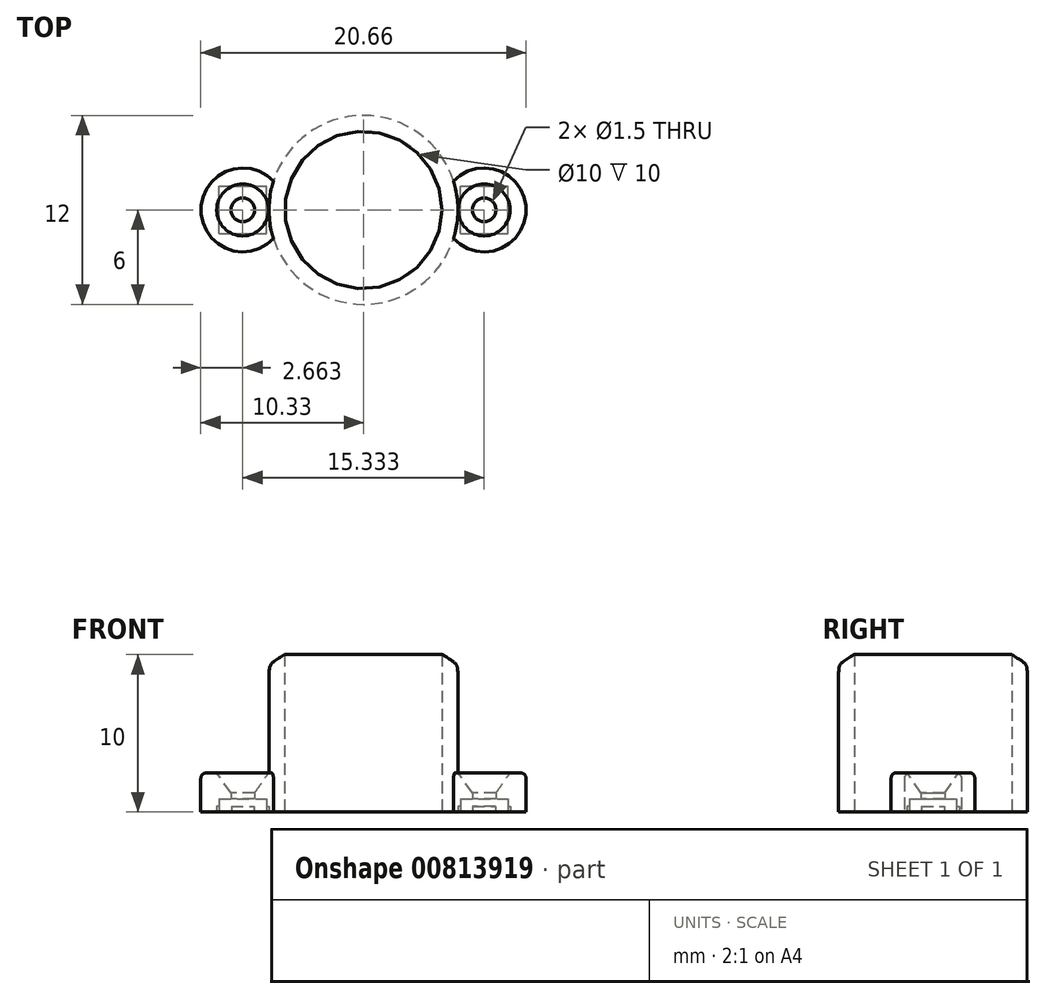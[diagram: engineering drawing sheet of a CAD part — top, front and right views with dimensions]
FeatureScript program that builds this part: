
annotation { "Feature Type Name" : "Feature", "Feature Type Description" : "" }
export const myFeature = defineFeature(function(context is Context, id is Id, definition is map)
    precondition{}
    {
        {
            assignVariable(context, id + "F0", {"name" : "Well", "anyValue" : 10 * mm});
        }
        {
            assignVariable(context, id + "F1", {"name" : "WellHeight", "anyValue" : getVariable(context, 'Well')});
        }
        {
            assignVariable(context, id + "F2", {"name" : "RimHeight", "anyValue" : getVariable(context, 'WellHeight') * 0.25});
        }
        {
            assignVariable(context, id + "F3", {"name" : "Hole", "anyValue" : getVariable(context, 'Well') * 0.15});
        }
        {
            var Q0;
            Q0=qCreatedBy(makeId("Top.planeOp"),FACE);
            var sketch = newSketch(context, id + "F4", { "sketchPlane" : qUnion([Q0])});
            skCircle(sketch, "E0", {"center": v(0, 0) * mm, "radius": 9.33 * mm});
            skCircle(sketch, "E1", {"center": v(0, 0) * mm, "radius": 6 * mm});
            skCircle(sketch, "E2", {"center": v(0, 0) * mm, "radius": 5 * mm});
            skSolve(sketch);
        }
        {
            var Q0;
            Q0=qCreatedBy(makeId("Top.planeOp"),FACE);
            var sketch = newSketch(context, id + "F5", { "sketchPlane" : qUnion([Q0])});
            skCircle(sketch, "E3", {"center": v(0, 0) * mm, "radius": 7.67 * mm});
            skCircle(sketch, "E4", {"center": v(-7.67, 0) * mm, "radius": 0.75 * mm});
            skCircle(sketch, "E5", {"center": v(7.67, 0) * mm, "radius": 0.75 * mm});
            skLineSegment(sketch, "E6.bottom", {"start": v(6.17, -1.5) * mm, "end": v(9.17, -1.5) * mm});
            skLineSegment(sketch, "E6.top", {"start": v(6.17, 1.5) * mm, "end": v(9.17, 1.5) * mm});
            skLineSegment(sketch, "E6.left", {"start": v(6.17, -1.5) * mm, "end": v(6.17, 1.5) * mm});
            skLineSegment(sketch, "E6.right", {"start": v(9.17, -1.5) * mm, "end": v(9.17, 1.5) * mm});
            skLineSegment(sketch, "E7.bottom", {"start": v(-9.17, -1.5) * mm, "end": v(-6.17, -1.5) * mm});
            skLineSegment(sketch, "E7.top", {"start": v(-9.17, 1.5) * mm, "end": v(-6.17, 1.5) * mm});
            skLineSegment(sketch, "E7.left", {"start": v(-9.17, -1.5) * mm, "end": v(-9.17, 1.5) * mm});
            skLineSegment(sketch, "E7.right", {"start": v(-6.17, -1.5) * mm, "end": v(-6.17, 1.5) * mm});
            skSolve(sketch);
        }
        {
            var Q0;
            Q0=qCreatedBy(makeId("Top.planeOp"),FACE);
            var sketch = newSketch(context, id + "F6", { "sketchPlane" : qUnion([Q0])});
            skCircle(sketch, "E8", {"center": v(-7.67, 0) * mm, "radius": 2.67 * mm});
            skCircle(sketch, "E9", {"center": v(7.67, 0) * mm, "radius": 2.67 * mm});
            skCircle(sketch, "E10", {"center": v(-7.67, 0) * mm, "radius": 1.67 * mm});
            skCircle(sketch, "E11", {"center": v(7.67, 0) * mm, "radius": 1.67 * mm});
            skSolve(sketch);
        }
        {
            var Q0;
            Q0=makeQuery(id+"F4.imprint","IMPRINT",FACE,{"disambiguationData":[TD([[makeQuery(id+"F4.imprint","IMPRINT",EDGE,{"derivedFrom":sQuery(id+"F4.wireOp",EDGE,"E1")}),1.0]])]});
            extrude(context, id + "F7", {"entities" : qUnion([Q0]), "depth" : getVariable(context, 'WellHeight'), "offsetDistance" : 25.4 * mm});
        }
        {
            var Q0;
            Q0=makeQuery(id+"F6.imprint","IMPRINT",FACE,{"disambiguationData":[TD([[makeQuery(id+"F6.imprint","IMPRINT",EDGE,{"derivedFrom":sQuery(id+"F6.wireOp",EDGE,"E8")}),1.0]])]});
            var Q1;
            Q1=makeQuery(id+"F6.imprint","IMPRINT",FACE,{"disambiguationData":[TD([[makeQuery(id+"F6.imprint","IMPRINT",EDGE,{"derivedFrom":sQuery(id+"F6.wireOp",EDGE,"E9")}),1.0]])]});
            var Q2;
            Q2=makeQuery(id+"F6.imprint","IMPRINT",FACE,{"disambiguationData":[TD([[makeQuery(id+"F6.imprint","IMPRINT",EDGE,{"derivedFrom":sQuery(id+"F6.wireOp",EDGE,"E10")}),1.0]])]});
            var Q3;
            Q3=makeQuery(id+"F6.imprint","IMPRINT",FACE,{"disambiguationData":[TD([[makeQuery(id+"F6.imprint","IMPRINT",EDGE,{"derivedFrom":sQuery(id+"F6.wireOp",EDGE,"E11")}),1.0]])]});
            extrude(context, id + "F8", {"entities" : qUnion([Q0, Q1, Q2, Q3]), "operationType" : NewBodyOperationType.ADD, "depth" : getVariable(context, 'RimHeight'), "offsetDistance" : 25.4 * mm});
        }
        {
            var Q0;
            Q0=makeQuery(id+"F7.opExtrude","CAP_EDGE",EDGE,{"disambiguationData":[OSD([sQuery(id+"F4.wireOp",EDGE,"E1")])],"isStart":false});
            fillet(context, id + "F9", {"entities" : qUnion([Q0]), "radius" : 2.03 * mm, "tangentPropagation" : true, "rho" : 0.8, "crossSection" : FilletCrossSection.CONIC, "allowEdgeOverflow" : false});
        }
        {
            var Q0;
            Q0=makeQuery(id+"F8.opExtrude","CAP_EDGE",EDGE,{"disambiguationData":[OSD([sQuery(id+"F6.wireOp",EDGE,"E9")])],"isStart":false});
            var Q1;
            Q1=makeQuery(id+"F8.opExtrude","CAP_EDGE",EDGE,{"disambiguationData":[OSD([sQuery(id+"F6.wireOp",EDGE,"E8")])],"isStart":false});
            fillet(context, id + "F10", {"entities" : qUnion([Q0, Q1]), "radius" : 0.43 * mm, "tangentPropagation" : true, "rho" : 0.5, "crossSection" : FilletCrossSection.CONIC, "allowEdgeOverflow" : false});
        }
        {
            var Q0;
            {var subQ0=sQuery(id+"F5.wireOp",EDGE,"E4");var subQ1=sQuery(id+"F5.wireOp",EDGE,"E3");var subQ2=makeQuery(id+"F5.imprint","INTERSECT",VERTEX,{"disambiguationData":[OD(0.0)],"derivedFrom":[subQ1,subQ0]});Q0=makeQuery(id+"F5.imprint","IMPRINT",FACE,{"disambiguationData":[TD([[makeQuery(id+"F5.imprint","IMPRINT",EDGE,{"disambiguationData":[TD([[subQ2,-1.0]])],"derivedFrom":subQ1}),-1.0]])]});}
            var Q1;
            {var subQ0=sQuery(id+"F5.wireOp",EDGE,"E4");var subQ1=sQuery(id+"F5.wireOp",EDGE,"E3");var subQ2=makeQuery(id+"F5.imprint","INTERSECT",VERTEX,{"disambiguationData":[OD(0.0)],"derivedFrom":[subQ1,subQ0]});Q1=makeQuery(id+"F5.imprint","IMPRINT",FACE,{"disambiguationData":[TD([[makeQuery(id+"F5.imprint","IMPRINT",EDGE,{"disambiguationData":[TD([[subQ2,-1.0]])],"derivedFrom":subQ1}),1.0]])]});}
            var Q2;
            {var subQ0=sQuery(id+"F5.wireOp",EDGE,"E5");var subQ1=sQuery(id+"F5.wireOp",EDGE,"E3");var subQ2=makeQuery(id+"F5.imprint","INTERSECT",VERTEX,{"disambiguationData":[OD(0.0)],"derivedFrom":[subQ1,subQ0]});Q2=makeQuery(id+"F5.imprint","IMPRINT",FACE,{"disambiguationData":[TD([[makeQuery(id+"F5.imprint","IMPRINT",EDGE,{"disambiguationData":[TD([[subQ2,1.0]])],"derivedFrom":subQ1}),1.0]])]});}
            var Q3;
            {var subQ0=sQuery(id+"F5.wireOp",EDGE,"E5");var subQ1=sQuery(id+"F5.wireOp",EDGE,"E3");var subQ2=makeQuery(id+"F5.imprint","INTERSECT",VERTEX,{"disambiguationData":[OD(0.0)],"derivedFrom":[subQ1,subQ0]});Q3=makeQuery(id+"F5.imprint","IMPRINT",FACE,{"disambiguationData":[TD([[makeQuery(id+"F5.imprint","IMPRINT",EDGE,{"disambiguationData":[TD([[subQ2,1.0]])],"derivedFrom":subQ1}),-1.0]])]});}
            extrude(context, id + "F11", {"entities" : qUnion([Q0, Q1, Q2, Q3]), "operationType" : NewBodyOperationType.REMOVE, "depth" : getVariable(context, 'RimHeight'), "offsetDistance" : 25.4 * mm});
        }
        {
            var Q0;
            {var subQ0=sQuery(id+"F5.wireOp",EDGE,"E7.top");var subQ1=sQuery(id+"F5.wireOp",EDGE,"E4");var subQ2=makeQuery(id+"F5.imprint","INTERSECT",VERTEX,{"derivedFrom":[subQ1,subQ0]});Q0=makeQuery(id+"F5.imprint","IMPRINT",FACE,{"disambiguationData":[TD([[makeQuery(id+"F5.imprint","IMPRINT",EDGE,{"disambiguationData":[TD([[subQ2,-1.0]])],"derivedFrom":subQ1}),-1.0]])]});}
            var Q1;
            {var subQ0=sQuery(id+"F5.wireOp",EDGE,"E7.left");var subQ1=sQuery(id+"F5.wireOp",EDGE,"E4");var subQ2=makeQuery(id+"F5.imprint","INTERSECT",VERTEX,{"derivedFrom":[subQ1,subQ0]});Q1=makeQuery(id+"F5.imprint","IMPRINT",FACE,{"disambiguationData":[TD([[makeQuery(id+"F5.imprint","IMPRINT",EDGE,{"disambiguationData":[TD([[subQ2,-1.0]])],"derivedFrom":subQ1}),-1.0]])]});}
            var Q2;
            {var subQ0=sQuery(id+"F5.wireOp",EDGE,"E7.bottom");var subQ1=sQuery(id+"F5.wireOp",EDGE,"E3");var subQ2=makeQuery(id+"F5.imprint","INTERSECT",VERTEX,{"derivedFrom":[subQ1,subQ0]});Q2=makeQuery(id+"F5.imprint","IMPRINT",FACE,{"disambiguationData":[TD([[makeQuery(id+"F5.imprint","IMPRINT",EDGE,{"disambiguationData":[TD([[subQ2,1.0]])],"derivedFrom":subQ1}),1.0]])]});}
            var Q3;
            {var subQ0=sQuery(id+"F5.wireOp",EDGE,"E7.top");var subQ1=sQuery(id+"F5.wireOp",EDGE,"E3");var subQ2=makeQuery(id+"F5.imprint","INTERSECT",VERTEX,{"derivedFrom":[subQ1,subQ0]});Q3=makeQuery(id+"F5.imprint","IMPRINT",FACE,{"disambiguationData":[TD([[makeQuery(id+"F5.imprint","IMPRINT",EDGE,{"disambiguationData":[TD([[subQ2,-1.0]])],"derivedFrom":subQ1}),1.0]])]});}
            var Q4;
            {var subQ0=sQuery(id+"F5.wireOp",EDGE,"E6.right");var subQ1=sQuery(id+"F5.wireOp",EDGE,"E5");var subQ2=makeQuery(id+"F5.imprint","INTERSECT",VERTEX,{"derivedFrom":[subQ1,subQ0]});Q4=makeQuery(id+"F5.imprint","IMPRINT",FACE,{"disambiguationData":[TD([[makeQuery(id+"F5.imprint","IMPRINT",EDGE,{"disambiguationData":[TD([[subQ2,1.0]])],"derivedFrom":subQ1}),-1.0]])]});}
            var Q5;
            {var subQ0=sQuery(id+"F5.wireOp",EDGE,"E6.bottom");var subQ1=sQuery(id+"F5.wireOp",EDGE,"E3");var subQ2=makeQuery(id+"F5.imprint","INTERSECT",VERTEX,{"derivedFrom":[subQ1,subQ0]});Q5=makeQuery(id+"F5.imprint","IMPRINT",FACE,{"disambiguationData":[TD([[makeQuery(id+"F5.imprint","IMPRINT",EDGE,{"disambiguationData":[TD([[subQ2,-1.0]])],"derivedFrom":subQ1}),1.0]])]});}
            var Q6;
            {var subQ0=sQuery(id+"F5.wireOp",EDGE,"E6.top");var subQ1=sQuery(id+"F5.wireOp",EDGE,"E3");var subQ2=makeQuery(id+"F5.imprint","INTERSECT",VERTEX,{"derivedFrom":[subQ1,subQ0]});Q6=makeQuery(id+"F5.imprint","IMPRINT",FACE,{"disambiguationData":[TD([[makeQuery(id+"F5.imprint","IMPRINT",EDGE,{"disambiguationData":[TD([[subQ2,1.0]])],"derivedFrom":subQ1}),1.0]])]});}
            var Q7;
            {var subQ0=sQuery(id+"F5.wireOp",EDGE,"E6.top");var subQ1=sQuery(id+"F5.wireOp",EDGE,"E5");var subQ2=makeQuery(id+"F5.imprint","INTERSECT",VERTEX,{"derivedFrom":[subQ1,subQ0]});Q7=makeQuery(id+"F5.imprint","IMPRINT",FACE,{"disambiguationData":[TD([[makeQuery(id+"F5.imprint","IMPRINT",EDGE,{"disambiguationData":[TD([[subQ2,1.0]])],"derivedFrom":subQ1}),-1.0]])]});}
            extrude(context, id + "F12", {"entities" : qUnion([Q0, Q1, Q2, Q3, Q4, Q5, Q6, Q7]), "operationType" : NewBodyOperationType.REMOVE, "depth" : getVariable(context, 'RimHeight') / 3, "offsetDistance" : 25.4 * mm});
        }
        {
            var Q0;
            Q0=makeQuery(id+"F8.opExtrude","CAP_FACE",FACE,{"disambiguationData":[OSD([sQuery(id+"F6.wireOp",EDGE,"E8")])],"isStart":false});
            var sketch = newSketch(context, id + "F13", { "sketchPlane" : qUnion([Q0])});
            skPoint(sketch, "E12", {"position": v(-7.67, 0) * mm});
            skPoint(sketch, "E13", {"position": v(7.67, 0) * mm});
            skSolve(sketch);
        }
        {
            var Q0;
            Q0=sQuery(id+"F13.wireOp",VERTEX,"E12");
            var Q1;
            Q1=sQuery(id+"F13.wireOp",VERTEX,"E13");
            var Q2;
            Q2=makeQuery(id+"F7.opExtrude","SWEPT_BODY",BODY,{"disambiguationData":[OSD([sQuery(id+"F4.wireOp",EDGE,"E1"),sQuery(id+"F4.wireOp",EDGE,"E2")])]});
            hole(context, id + "F14", {"style" : HoleStyle.C_SINK, "endStyle" : HoleEndStyle.THROUGH, "holeDiameter" : getVariable(context, 'Hole'), "cSinkDiameter" : getVariable(context, 'Hole') * 2.2, "cSinkAngle" : 70 * degree, "majorDiameter" : 6.35 * mm, "isTappedThrough" : true, "tappedDepth" : 12.7 * mm, "tapClearance" : 3, "startFromSketch" : true, "locations" : qUnion([Q0, Q1]), "scope" : qUnion([Q2])});
        }
        {
            var Q0;
            Q0=makeQuery(id+"F6.imprint","IMPRINT",FACE,{"disambiguationData":[TD([[makeQuery(id+"F6.imprint","IMPRINT",EDGE,{"derivedFrom":sQuery(id+"F6.wireOp",EDGE,"E10")}),1.0]])]});
            var Q1;
            Q1=makeQuery(id+"F6.imprint","IMPRINT",FACE,{"disambiguationData":[TD([[makeQuery(id+"F6.imprint","IMPRINT",EDGE,{"derivedFrom":sQuery(id+"F6.wireOp",EDGE,"E11")}),1.0]])]});
            extrude(context, id + "F15", {"entities" : qUnion([Q0, Q1]), "operationType" : NewBodyOperationType.REMOVE, "depth" : getVariable(context, 'RimHeight') * 0.15, "offsetDistance" : 25.4 * mm});
        }
    });
